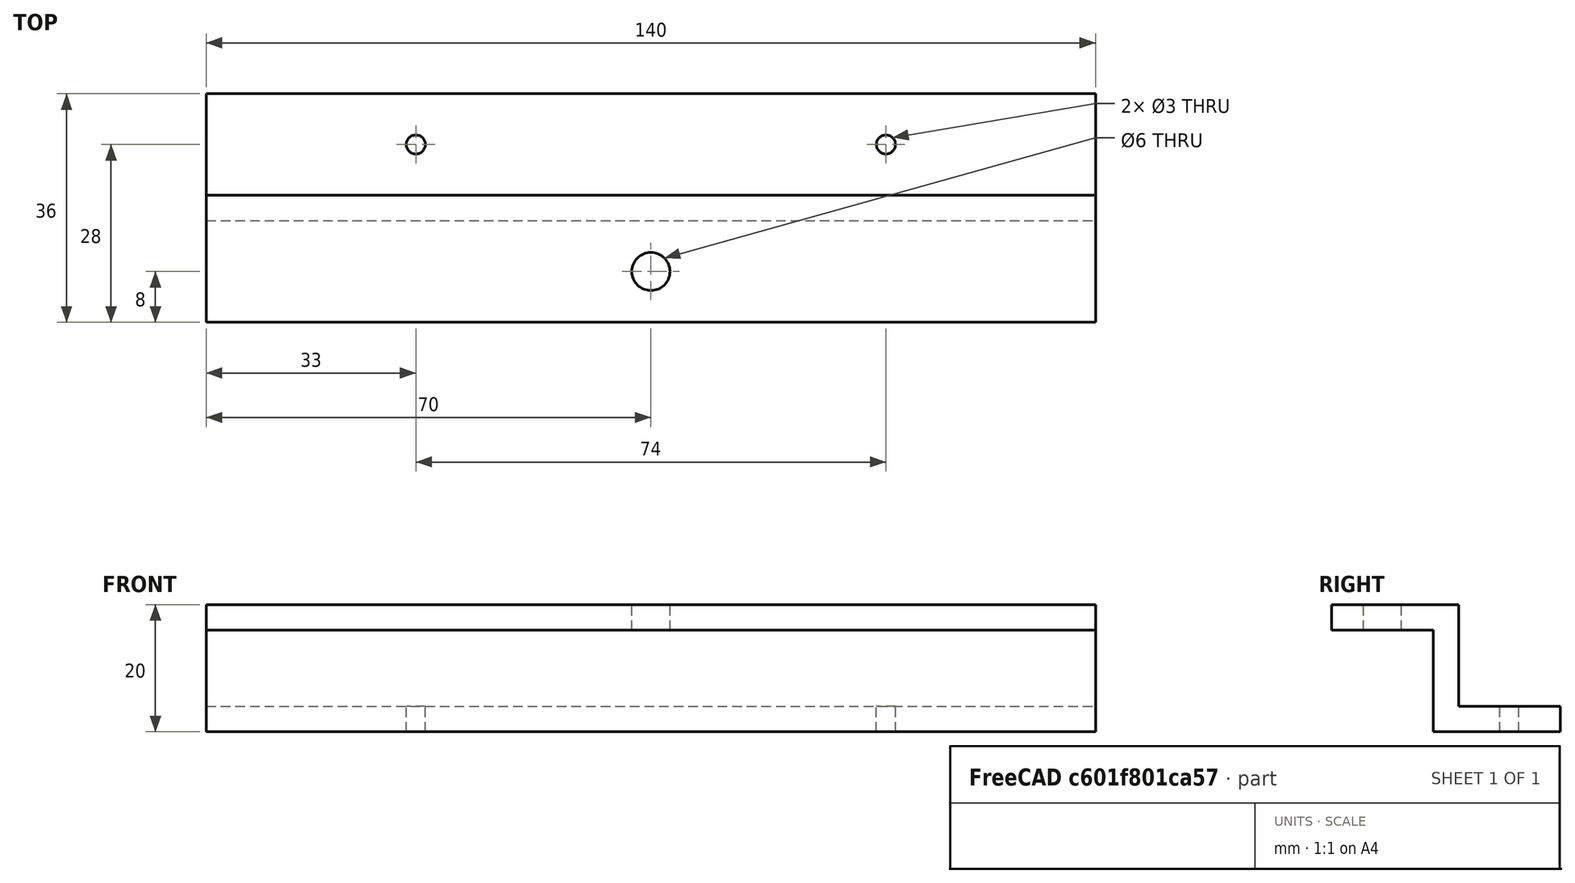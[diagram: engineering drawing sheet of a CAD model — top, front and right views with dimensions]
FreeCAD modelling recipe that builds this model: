
FCSTD DOCUMENT  (FreeCAD 0.15R4671 (Git))
Label: perfil Z derecho
License: All rights reserved
LicenseURL: http://en.wikipedia.org/wiki/All_rights_reserved
objects: Part::Box×3, Part::Cylinder×3, Part::MultiFuse×2, Part::Cut×1, App::DocumentObjectGroup×1
note: 9 computed .brp shape members not serialized (recipe doc carries the construction recipe); baked Part::Feature solids carry a one-line shape summary decoded from their .brp

FEATURE [Part::Box] Box  label="Perfil intermedio"
  Height = 20
  Length = 140
  Width = 4
FEATURE [Part::Box] Box001  label="Perfil inferior"
  Height = 4
  Length = 140
  Width = 20
FEATURE [Part::Box] Box002  label="Perfil superior"
  Height = 4
  Length = 140
  Placement = pos=(0,-16,16) rot=(0,0,1;0rad)
  Width = 20
FEATURE [Part::Cylinder] Cylinder  label="Agujero de metrica 3 trasero"
  Angle = 360
  Height = 4
  Placement = pos=(33,12,0) rot=(0,0,1;0rad)
  Radius = 1.5
FEATURE [Part::Cylinder] Cylinder001  label="Agujero de metrica 3 delantero"
  Angle = 360
  Height = 4
  Placement = pos=(107,12,0) rot=(0,0,1;0rad)
  Radius = 1.5
FEATURE [Part::Cylinder] Cylinder002  label="Agujero metrica 6"
  Angle = 360
  Height = 4
  Placement = pos=(70,-8,16) rot=(0,0,1;0rad)
  Radius = 3
FEATURE [Part::MultiFuse] Fusion  label="Perfil z"
  Shapes = -> [Box,Box001,Box002]
FEATURE [Part::MultiFuse] Fusion001  label="Perforaciones"
  Shapes = -> [Cylinder001,Cylinder,Cylinder002]
FEATURE [Part::Cut] Cut  label="Perfil derecho"
  Base = -> Fusion
  Tool = -> Fusion001
FEATURE [App::DocumentObjectGroup] Grupo  label="Perfil Z"
  Group = -> [Cut]
